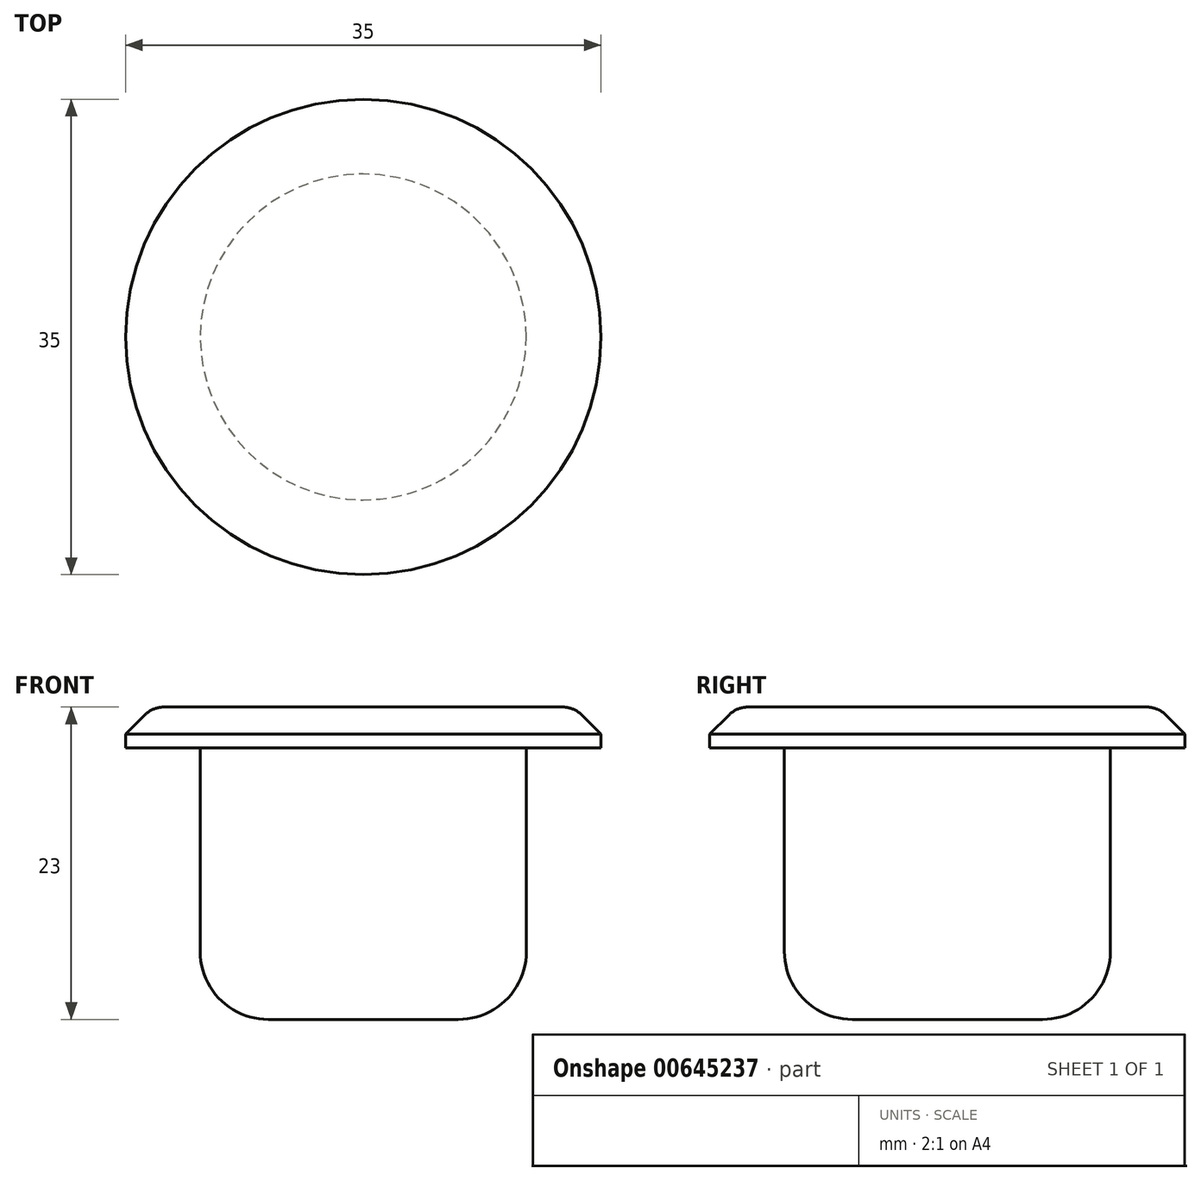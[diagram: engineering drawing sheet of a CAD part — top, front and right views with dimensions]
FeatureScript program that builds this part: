
annotation { "Feature Type Name" : "Feature", "Feature Type Description" : "" }
export const myFeature = defineFeature(function(context is Context, id is Id, definition is map)
    precondition{}
    {
        {
            var Q0;
            Q0=qCreatedBy(makeId("Top.planeOp"),FACE);
            var sketch = newSketch(context, id + "F0", { "sketchPlane" : qUnion([Q0])});
            skCircle(sketch, "E0", {"center": v(0, 0) * mm, "radius": 12 * mm});
            skSolve(sketch);
        }
        {
            var Q0;
            Q0=makeQuery(id+"F0.imprint","IMPRINT",FACE,{"disambiguationData":[TD([[makeQuery(id+"F0.imprint","IMPRINT",EDGE,{"derivedFrom":sQuery(id+"F0.wireOp",EDGE,"E0")}),1.0]])]});
            extrude(context, id + "F1", {"entities" : qUnion([Q0]), "depth" : 20 * mm, "offsetDistance" : 25 * mm});
        }
        {
            var Q0;
            Q0=makeQuery(id+"F1.opExtrude","CAP_FACE",FACE,{"disambiguationData":[OSD([sQuery(id+"F0.wireOp",EDGE,"E0")])],"isStart":false});
            var sketch = newSketch(context, id + "F2", { "sketchPlane" : qUnion([Q0])});
            skCircle(sketch, "E1", {"center": v(0, 0) * mm, "radius": 17.5 * mm});
            skSolve(sketch);
        }
        {
            var Q0;
            Q0 = qSketchRegion(id + "F2", true);
            extrude(context, id + "F3", {"entities" : qUnion([Q0]), "depth" : 3 * mm, "offsetDistance" : 25 * mm});
        }
        {
            var Q0;
            Q0=makeQuery(id+"F1.opExtrude","CAP_EDGE",EDGE,{"disambiguationData":[OSD([sQuery(id+"F0.wireOp",EDGE,"E0")])],"isStart":true});
            fillet(context, id + "F4", {"entities" : qUnion([Q0]), "radius" : 5 * mm, "tangentPropagation" : true, "allowEdgeOverflow" : false});
        }
        {
            var Q0;
            Q0=makeQuery(id+"F3.opExtrude","CAP_EDGE",EDGE,{"disambiguationData":[OSD([sQuery(id+"F2.wireOp",EDGE,"E1")])],"isStart":false});
            chamfer(context, id + "F5", {"entities" : qUnion([Q0]), "width" : 2 * mm, "tangentPropagation" : true});
        }
        {
            var Q0;
            {var subQ0=sQuery(id+"F2.wireOp",EDGE,"E1");Q0=makeQuery(id+"F5.opChamfer","BLEND_EDGE",EDGE,{"blendedFrom":[makeQuery(id+"F3.opExtrude","CAP_EDGE",EDGE,{"disambiguationData":[OSD([subQ0])],"isStart":false}),makeQuery(id+"F3.opExtrude","CAP_FACE",FACE,{"disambiguationData":[OSD([subQ0])],"isStart":false})],"blendedInto":[makeQuery(id+"F3.opExtrude","CAP_FACE",FACE,{"disambiguationData":[OSD([subQ0])],"isStart":false})]});}
            var Q1;
            Q1=makeQuery(id+"F4.opFillet","BLEND_FACE",FACE,{"disambiguationData":[OSD([sQuery(id+"F0.wireOp",EDGE,"E0")])]});
            fillet(context, id + "F6", {"entities" : qUnion([Q0, Q1]), "radius" : 2 * mm, "tangentPropagation" : true, "allowEdgeOverflow" : false});
        }
    });
